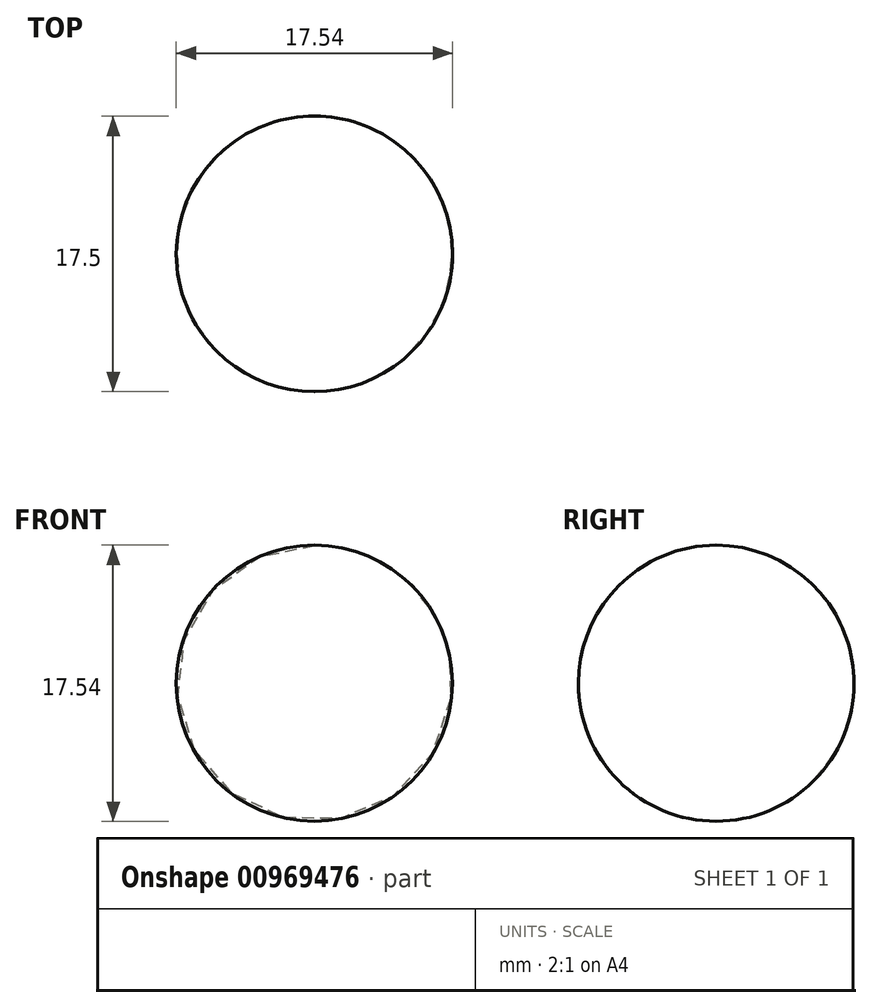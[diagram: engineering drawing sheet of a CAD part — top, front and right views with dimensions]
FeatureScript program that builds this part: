
annotation { "Feature Type Name" : "Feature", "Feature Type Description" : "" }
export const myFeature = defineFeature(function(context is Context, id is Id, definition is map)
    precondition{}
    {
        {
            var Q0;
            Q0=qCreatedBy(makeId("Top.planeOp"),FACE);
            var sketch = newSketch(context, id + "F0", { "sketchPlane" : qUnion([Q0])});
            skLineSegment(sketch, "E0", {"start": v(0, 0) * mm, "end": v(0, 17.5) * mm});
            skArc(sketch, "E1", {"start": v(0, 0) * mm, "mid": v(8.73, 8.75) * mm, "end": v(0, 17.5) * mm});
            skSolve(sketch);
        }
        {
            var Q0;
            Q0=makeQuery(id+"F0.imprint","IMPRINT",FACE,{"disambiguationData":[TD([[makeQuery(id+"F0.imprint","IMPRINT",EDGE,{"derivedFrom":sQuery(id+"F0.wireOp",EDGE,"E0")}),-1.0]])]});
            var Q1;
            Q1=sQuery(id+"F0.wireOp",EDGE,"E0");
            revolve(context, id + "F1", {"surfaceOperationType" : NewSurfaceOperationType.NEW, "entities" : qUnion([Q0]), "axis" : qUnion([Q1]), "revolveType" : RevolveType.FULL});
        }
    });
